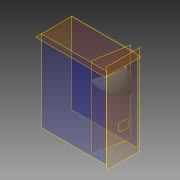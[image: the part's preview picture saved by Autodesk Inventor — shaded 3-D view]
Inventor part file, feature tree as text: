
AUTODESK INVENTOR PART (.ipt)
format: ipt  version: 2014 (Build 180170000, 170)  size: 1,329,664 bytes
history: native  units: mm
features: other x11, extrude x6, sketch x6, fillet x5, projected_geometry x2
ambient origin geometry x8: Origin, YZ Plane, XZ Plane, XY Plane, X Axis, Y Axis, Z Axis, Center Point
bodies: Body1 (feature_tree)
feature tree (30):
  other  "exoskeletal-main.ipt"
  extrude  "押し出し1"  Depth=10.0mm
  other  "厚み6"
  other  "厚み5"
  extrude  "押し出し3"  Depth=70.0mm TaperAngle=0.0deg
  other  "作業平面75"
  extrude  "押し出し4"  Depth=0.8mm
  other  "作業平面76"
  extrude  "押し出し5"  Depth=3.0mm TaperAngle=0.0deg
  extrude  "押し出し6"  Depth=8.672mm
  extrude  "押し出し7"  Depth=20.0mm
  fillet  "フィレット5"  Radius=12.0mm
  fillet  "フィレット14"  Radius=6.0mm
  fillet  "フィレット17"  Radius=7.5mm
  fillet  "フィレット20"  Radius=7.5mm
  fillet  "フィレット21"  Radius=6.0mm
  other  "ソリッド1::exoskeletal-main.ipt"
  other  "TaggingFeature1"
  sketch  "スケッチ17"
  other  "作業平面1"
  other  "作業平面6"
  sketch  "スケッチ2"
  projected_geometry  "投影ループ1"
  sketch  "スケッチ5"
  sketch  "スケッチ6"
  sketch  "スケッチ7"
  projected_geometry  "投影ループ2"
  sketch  "スケッチ8"
  other  "ソリッド1"
  other  "ソリッド11"
